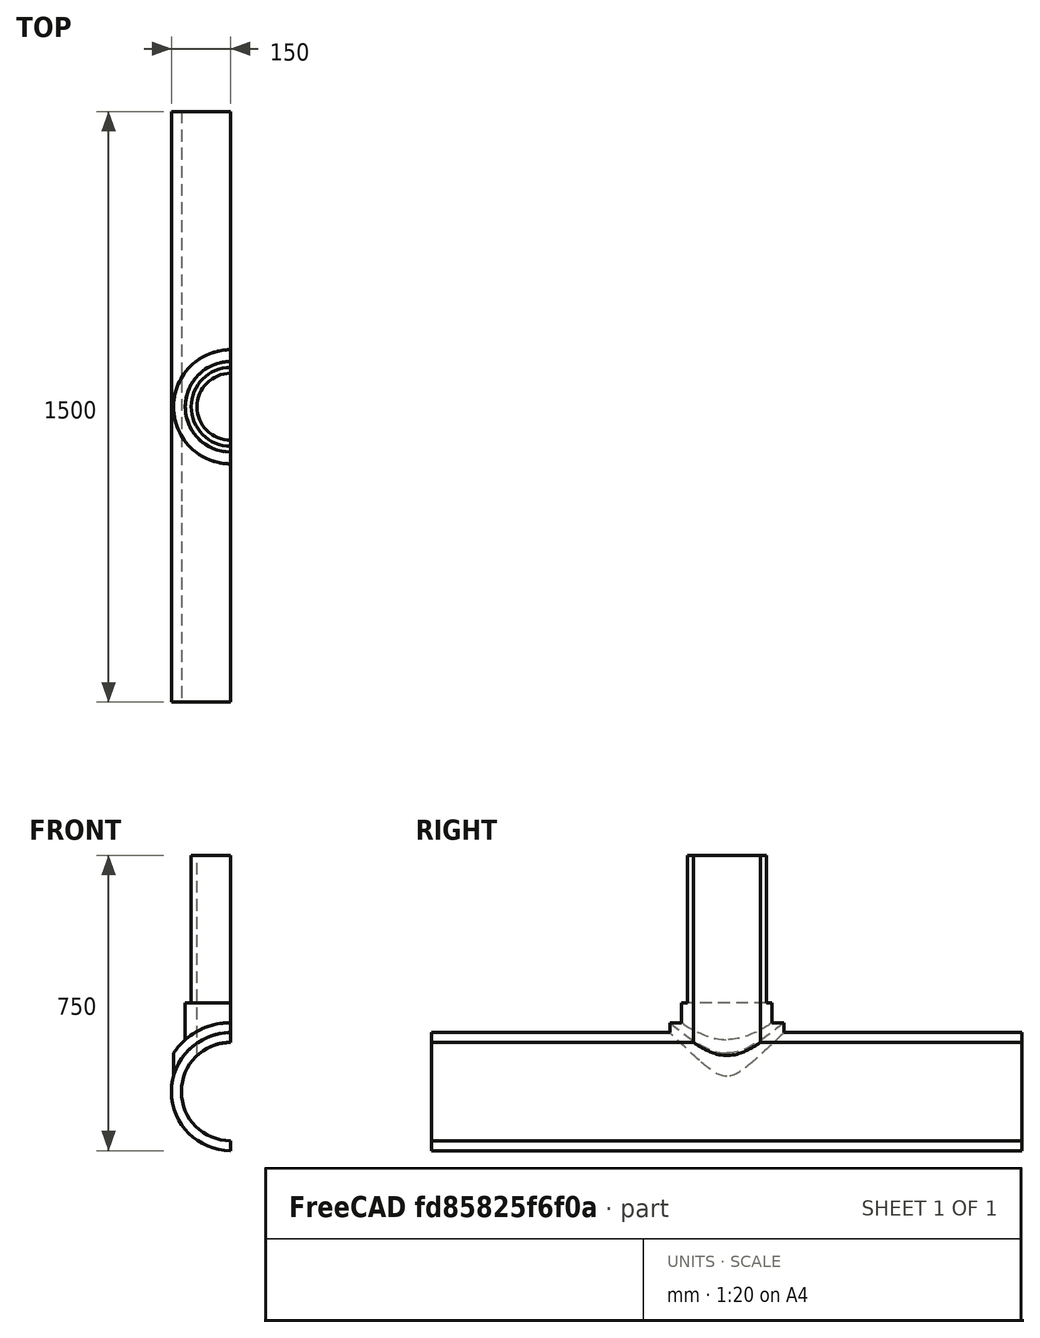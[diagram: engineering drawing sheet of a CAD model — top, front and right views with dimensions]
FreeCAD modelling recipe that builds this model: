
FCSTD DOCUMENT  (FreeCAD 0.16RUnknown)
Label: T-pipe transient thermo FEM model 2
License: All rights reserved
LicenseURL: http://en.wikipedia.org/wiki/All_rights_reserved
objects: Part::Cylinder×14, Part::Cut×9, Part::MultiFuse×5, Part::Box×4, Fem::ConstraintDisplacement×3, Fem::ConstraintHeatflux×2, Fem::FemSolverObjectPython×1, Fem::FemMeshShapeNetgenObject×1, App::MaterialObjectPython×1, Fem::ConstraintInitialTemperature×1, Fem::FemAnalysisPython×1
note: 32 computed .brp shape members not serialized (recipe doc carries the construction recipe); baked Part::Feature solids carry a one-line shape summary decoded from their .brp

FEATURE [Part::Cylinder] Cylinder
  Angle = 360
  Height = 600
  Radius = 100
FEATURE [Part::Cylinder] Cylinder001
  Angle = 360
  Height = 1500
  Placement = pos=(0,750,0) rot=(1,0,0;1.5708rad)
  Radius = 150
FEATURE [Part::Cylinder] Cylinder002
  Angle = 360
  Height = 225
  Radius = 115
FEATURE [Part::Cylinder] Cylinder003
  Angle = 360
  Height = 400
  Placement = pos=(0,200,0) rot=(1,0,0;1.5708rad)
  Radius = 175
FEATURE [Part::Cylinder] Cylinder004
  Angle = 360
  Height = 600
  Radius = 145
FEATURE [Part::Cylinder] Cylinder005
  Angle = 360
  Height = 600
  Radius = 300
FEATURE [Part::Cut] Cut
  Base = -> Cylinder005
  Tool = -> Cylinder004
FEATURE [Part::Cut] Cut001
  Base = -> Cylinder003
  Tool = -> Cut
FEATURE [Part::Box] Box  label="Cube"
  Height = 500
  Length = 500
  Placement = pos=(-226,-279,-480) rot=(0,0,1;0rad)
  Width = 500
FEATURE [Part::Cut] Cut002
  Base = -> Cut001
  Tool = -> Box
FEATURE [Part::MultiFuse] Fusion
  Shapes = -> [Cut002,Cylinder002,Cylinder001,Cylinder]
FEATURE [Part::Cylinder] Cylinder006
  Angle = 360
  Height = 600
  Radius = 85
FEATURE [Part::Cut] Cut003
  Base = -> Fusion
  Tool = -> Cylinder006
FEATURE [Part::Cylinder] Cylinder007
  Angle = 360
  Height = 1500
  Placement = pos=(0,750,0) rot=(1,0,0;1.5708rad)
  Radius = 125
FEATURE [Part::Cut] Cut004
  Base = -> Cut003
  Tool = -> Cylinder007
FEATURE [Part::Cylinder] Cylinder008
  Angle = 360
  Height = 100
  Placement = pos=(0,-150,0) rot=(1,0,0;1.5708rad)
  Radius = 150
FEATURE [Part::Cylinder] Cylinder009
  Angle = 360
  Height = 100
  Placement = pos=(0,250,0) rot=(1,0,0;1.5708rad)
  Radius = 150
FEATURE [Part::MultiFuse] Fusion001
  Shapes = -> [Cylinder008,Cylinder009,Cut004]
FEATURE [Part::Cylinder] Cylinder010
  Angle = 360
  Height = 80
  Placement = pos=(0,-70,0) rot=(1,0,0;1.5708rad)
  Radius = 150
FEATURE [Part::Cylinder] Cylinder011
  Angle = 360
  Height = 80
  Placement = pos=(0,150,0) rot=(1,0,0;1.5708rad)
  Radius = 150
FEATURE [Part::MultiFuse] Fusion002
  Shapes = -> [Cylinder010,Cylinder011]
FEATURE [Part::Box] Box001  label="Cube001"
  Height = 300
  Length = 500
  Placement = pos=(-250,-250,80) rot=(0,0,1;0rad)
  Width = 500
FEATURE [Part::Cut] Cut005
  Base = -> Fusion002
  Tool = -> Box001
FEATURE [Part::MultiFuse] Fusion003
  Shapes = -> [Fusion001,Cut005]
FEATURE [Part::Cylinder] Cylinder012
  Angle = 360
  Height = 140
  Placement = pos=(0,70,0) rot=(1,0,0;1.5708rad)
  Radius = 150
FEATURE [Part::Box] Box002  label="Cube002"
  Height = 300
  Length = 500
  Placement = pos=(-250,-250,38) rot=(0,0,1;0rad)
  Width = 500
FEATURE [Part::Cut] Cut006
  Base = -> Cylinder012
  Tool = -> Box002
FEATURE [Part::MultiFuse] Fusion004
  Shapes = -> [Fusion003,Cut006]
FEATURE [Part::Cylinder] Cylinder013
  Angle = 360
  Height = 1500
  Placement = pos=(0,750,0) rot=(1,0,0;1.5708rad)
  Radius = 125
FEATURE [Part::Cut] Cut007
  Base = -> Fusion004
  Tool = -> Cylinder013
FEATURE [Part::Box] Box003  label="Cube003"
  Height = 1000
  Length = 500
  Placement = pos=(0,-896,-320) rot=(0,0,1;0rad)
  Width = 1700
FEATURE [Part::Cut] Cut008
  Base = -> Cut007
  Tool = -> Box003
FEATURE [Fem::FemSolverObjectPython] CalculiX  # FEM object (typed FeaturePython)
  AnalysisType = 2
  EigenmodeHighLimit = 1000000
  EigenmodeLowLimit = 0
  EndTime = 20000
  InitialTimeStep = 25
  MatrixSolverType = 0
  Maxiterations = 2000
  NonLinearGeometry = false
  NumCpus = 4
  NumberOfEigenmodes = 10
  SolverType = FemSolverCalculix
  SteadyState = false
FEATURE [Fem::FemMeshShapeNetgenObject] Cut008_Mesh
  Fineness = 2
  GrowthRate = 0.3
  MaxSize = 1000
  NbSegsPerEdge = 1
  NbSegsPerRadius = 2
  Optimize = true
  SecondOrder = true
  Shape = -> Cut008
FEATURE [App::MaterialObjectPython] MechanicalMaterial  # material (typed FeaturePython)
  Material = Density=7900.0 kg/m^3,+10 more (map truncated)
FEATURE [Fem::ConstraintDisplacement] FemConstraintDisplacement  label="FemConstraintDisplacementX"
  NormalDirection = (1,0,0)
  Normals = (27) [(1,0,0),(1,0,0),(1,0,0),(1,0,0),(1,0,0),(1,0,0),(1,0,0),(1,0,0),(1,0,0),(1,0,0),(1,0,0),(1,0,0),(1,0,0),(1,0,0),(1,0,0),(1,0,0),(1,0,0),(1,0,0),+9 more]
  Points = (27) [(0,-85,125),(0,-85,600),(0,85,125),(0,750,-150),(0,750,-141.667),(0,750,-133.333),(0,750,-125),(0,450,-150),(0,450,-141.667),(0,450,-133.333),+17 more]
  References = -> [Cut008]
  rotxFix = false
  rotxFree = true
  rotyFix = false
  rotyFree = true
  rotzFix = false
  rotzFree = true
  xDisplacement = 0
  xFix = true
  xFree = false
  xRotation = 0
  yDisplacement = 0
  yFix = false
  yFree = true
  yRotation = 0
  zDisplacement = 0
  zFix = false
  zFree = true
  zRotation = 0
FEATURE [Fem::ConstraintDisplacement] FemConstraintDisplacement001  label="FemConstraintDisplacementY"
  NormalDirection = (0,-1,0)
  Normals = (2) [(0,-1,2.22045e-16),(0,-1,2.22045e-16)]
  Points = (2) [(0,-750,-150),(0,-750,150)]
  References = -> [Cut008]
  Scale = 16
  rotxFix = false
  rotxFree = true
  rotyFix = false
  rotyFree = true
  rotzFix = false
  rotzFree = true
  xDisplacement = 0
  xFix = false
  xFree = true
  xRotation = 0
  yDisplacement = 0
  yFix = true
  yFree = false
  yRotation = 0
  zDisplacement = 0
  zFix = false
  zFree = true
  zRotation = 0
FEATURE [Fem::ConstraintDisplacement] FemConstraintDisplacement002  label="FemConstraintDisplacementZ"
  NormalDirection = (0,0,1)
  Normals = (2) [(0,0,1),(0,0,1)]
  Points = (2) [(0,-100,600),(0,100,600)]
  References = -> [Cut008]
  Scale = 13
  rotxFix = false
  rotxFree = true
  rotyFix = false
  rotyFree = true
  rotzFix = false
  rotzFree = true
  xDisplacement = 0
  xFix = false
  xFree = true
  xRotation = 0
  yDisplacement = 0
  yFix = false
  yFree = true
  yRotation = 0
  zDisplacement = 0
  zFix = true
  zFree = false
  zRotation = 0
FEATURE [Fem::ConstraintInitialTemperature] FemConstraintInitialTemperature
  NormalDirection = (0,0,1)
  initialTemperature = 300
FEATURE [Fem::ConstraintHeatflux] FemConstraintHeatflux001
  AmbientTemp = 980
  FilmCoef = 500
  NormalDirection = (-1,0,0)
  Normals = (78) [(6.12323e-17,2.22045e-16,1),(-0.866025,1.11022e-16,0.5),(-0.866025,-1.11022e-16,-0.5),(-1.83697e-16,-2.22045e-16,-1),(6.12323e-17,2.22045e-16,1),+73 more]
  Points = (78) [(9.18485e-15,250,150),(-129.904,250,75),(-129.904,250,-75),(-2.75546e-14,250,-150),(9.18485e-15,216.667,150),(-129.904,216.667,75),+72 more]
  References = -> [Cut008]
  Scale = 18
FEATURE [Fem::ConstraintHeatflux] FemConstraintHeatflux
  AmbientTemp = 300
  FilmCoef = 10
  NormalDirection = (1,0,0)
  Normals = (68) [(-6.12323e-17,-2.22045e-16,-1),(0.866025,-1.11022e-16,-0.5),(0.866025,1.11022e-16,0.5),(1.83697e-16,2.22045e-16,1),(-6.12323e-17,-2.22045e-16,-1),+63 more]
  Points = (68) [(7.65404e-15,-250,125),(-108.253,-250,62.5),(-108.253,-250,-62.5),(-2.29621e-14,-250,-125),(7.65404e-15,-416.667,125),(-108.253,-416.667,62.5),+62 more]
  References = -> [Cut008]
  Scale = 23
FEATURE [Fem::FemAnalysisPython] MechanicalAnalysis  # FEM object (typed FeaturePython)
  Member = -> [CalculiX,Cut008_Mesh,MechanicalMaterial,FemConstraintDisplacement,FemConstraintDisplacement001,FemConstraintDisplacement002,FemConstraintInitialTemperature,FemConstraintHeatflux001,FemConstraintHeatflux]
